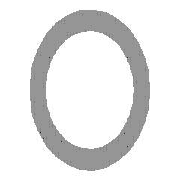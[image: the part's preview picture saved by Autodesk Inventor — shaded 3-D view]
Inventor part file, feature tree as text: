
AUTODESK INVENTOR PART (.ipt)
format: ipt  version: 2021 (Build 250183000, 183)  size: 786,944 bytes
history: native  units: mm (DEFAULTED — no unit token found)
features: other x16, plane x5, sketch x3, sweep x1, split x1
ambient origin geometry x8: Origin, YZ Plane, XZ Plane, XY Plane, X Axis, Y Axis, Z Axis, Center Point
bodies: Solid1 (feature_tree)
feature tree (26):
  parser-record x2  (decoder bookkeeping rows leaked as tree rows — omitted from the tree; the rows remain in map.json)
  other  "Driven Length"
  other  "Plano inicial"
  other  "Plano final"
  other  "Trayectoria de barrido"
  plane  "Plano de trabajo de orientación"
  sweep  "Cuerpo"
  plane  "Plano de trabajo7"
  split  "Dividir3"
  plane  "Plano de trabajo8"
  plane  "Plano de trabajo9"
  sketch  "Sketch3"  dims[d0=26.67mm d1=2.8702mm]
  plane  "Work Plane3"
  sketch  "Sketch4"  dims[d4=-0.0mm]
  sketch  "Boceto7"  dims[d5=1118.571117mm d6=90.0deg d7=1118.571117mm d8=0.0mm d9=0.0mm d38=16.002mm d39=254.157378mm d64=0.0mm d65=90.0deg d66=0.0mm d67=90.0deg d128=5.0mm d129=0.0mm d130=5.0mm d131=0.0mm]
  other  "Sup36"
  other  "Sup83"
  other  "Sup84"
  other  "Sólido28"
  other  "SuperficieSolevación3"
  other  "Sup82"
  other  "Superficie de contorno53"
  other  "Superficie de contorno54"
  other  "Marco_Bicicleta.iam"
  other  "Esqueleto_estructura:1"
note: 1 file-system path scrubbed to <path> (originals preserved in map.json)
